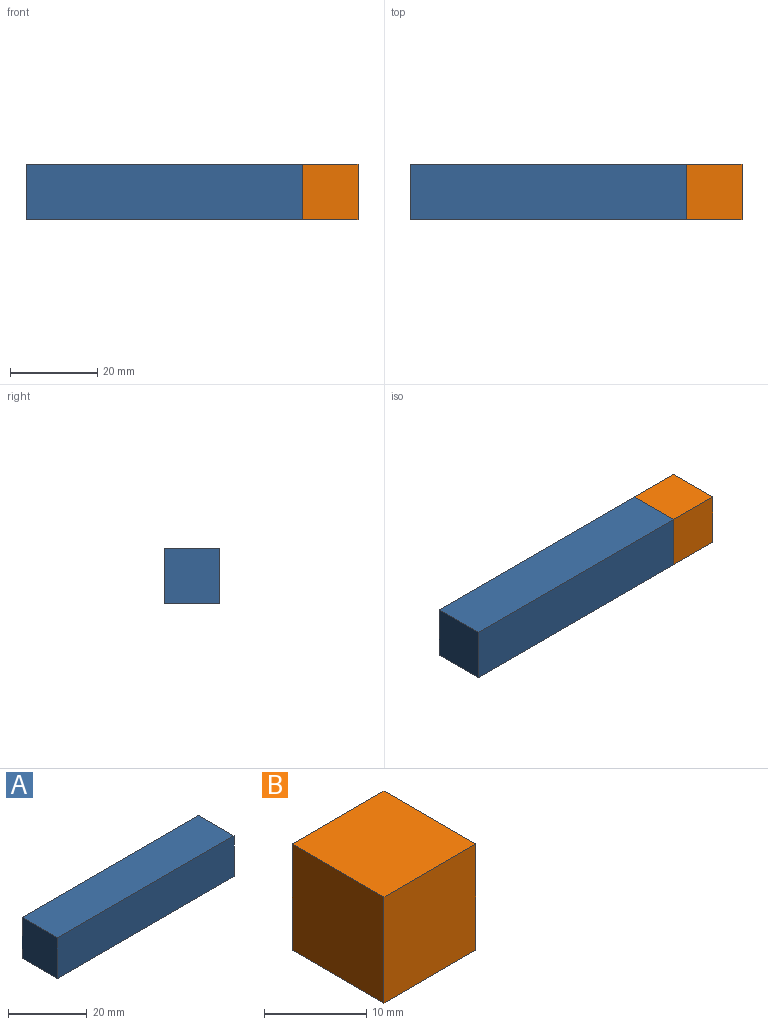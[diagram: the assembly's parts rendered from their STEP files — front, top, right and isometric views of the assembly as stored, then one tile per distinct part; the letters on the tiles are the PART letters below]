
ASSEMBLY  parts=2 mates=1
PART A: 6 faces, bbox 63.5x12.7x12.7 mm
  f0: plane 63.5x12.7mm, normal (0,0,-1), area 806.5mm2, adj f1,f3,f4,f5
  f1: plane 12.7x12.7mm, normal (1,0,0), area 161.3mm2, adj f0,f2,f4,f5
  f2: plane 63.5x12.7mm, normal (0,0,1), area 806.5mm2, adj f1,f3,f4,f5
  f3: plane 12.7x12.7mm, normal (-1,0,0), area 161.3mm2, adj f0,f2,f4,f5
  f4: plane 63.5x12.7mm, normal (0,-1,0), area 806.5mm2, adj f0,f1,f2,f3
  f5: plane 63.5x12.7mm, normal (0,1,0), area 806.5mm2, adj f0,f1,f2,f3
PART B: 6 faces, bbox 12.7x12.7x12.7 mm
  f0: plane 12.7x12.7mm, normal (0,0,-1), area 161.3mm2, adj f1,f3,f4,f5
  f1: plane 12.7x12.7mm, normal (1,0,0), area 161.3mm2, adj f0,f2,f4,f5
  f2: plane 12.7x12.7mm, normal (0,0,1), area 161.3mm2, adj f1,f3,f4,f5
  f3: plane 12.7x12.7mm, normal (-1,0,0), area 161.3mm2, adj f0,f2,f4,f5
  f4: plane 12.7x12.7mm, normal (0,-1,0), area 161.3mm2, adj f0,f1,f2,f3
  f5: plane 12.7x12.7mm, normal (0,1,0), area 161.3mm2, adj f0,f1,f2,f3
PLACE A t=(-31.86,-2,-13.5)mm
PLACE B rot(axis=(0,1,0),180deg) t=(2.93,-2,-28.54)mm
MATE slider B.f1 <-> A.f1  axis (-1,0,0) through (-3.42,-8.35,-57.11)mm
